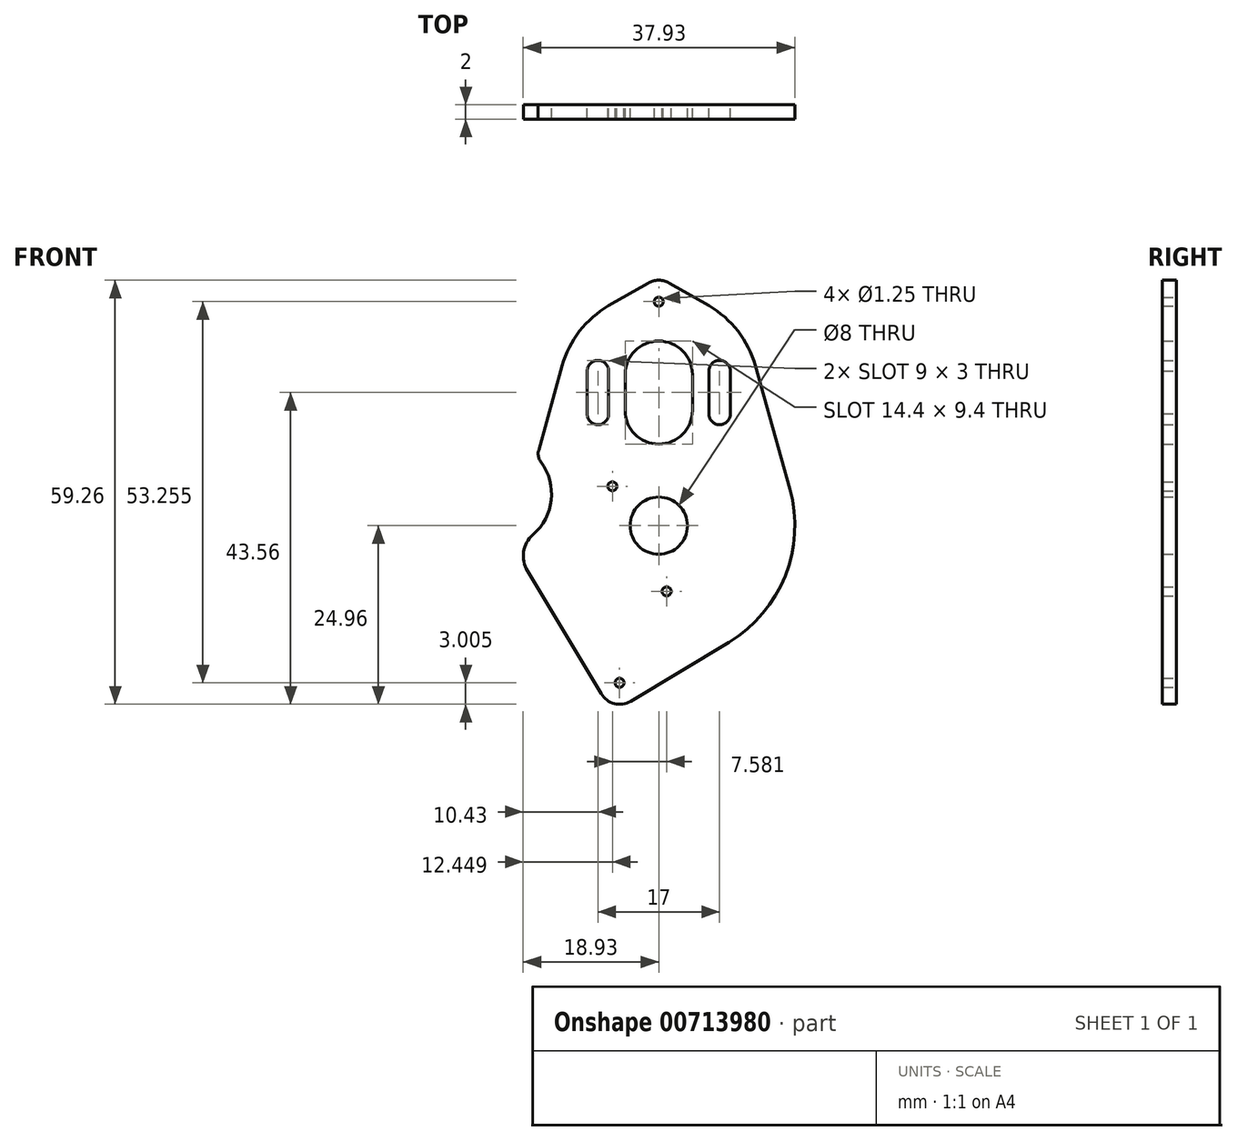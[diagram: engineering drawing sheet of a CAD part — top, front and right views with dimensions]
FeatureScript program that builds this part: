
annotation { "Feature Type Name" : "Feature", "Feature Type Description" : "" }
export const myFeature = defineFeature(function(context is Context, id is Id, definition is map)
    precondition{}
    {
        {
            var Q0;
            Q0=qCreatedBy(makeId("Front.planeOp"),FACE);
            var sketch = newSketch(context, id + "F0", { "sketchPlane" : qUnion([Q0])});
            skCircle(sketch, "E0", {"center": v(0, 0) * mm, "radius": 4 * mm});
            skArc(sketch, "E1", {"start": v(9.79, -16.29) * mm, "mid": v(17.65, -7.03) * mm, "end": v(18.3, 5.1) * mm});
            skLineSegment(sketch, "E2", {"start": v(-18.36, -6.34) * mm, "end": v(-8.05, -23.5) * mm});
            skLineSegment(sketch, "E3", {"start": v(-3.93, -24.53) * mm, "end": v(9.79, -16.29) * mm});
            skCircle(sketch, "E4", {"center": v(0, 0) * mm, "radius": 9.25 * mm, "construction": true});
            skCircle(sketch, "E5", {"center": v(1.1, -9.18) * mm, "radius": 0.62 * mm});
            skCircle(sketch, "E6", {"center": v(0, 0) * mm, "radius": 8.5 * mm, "construction": true});
            skCircle(sketch, "E7", {"center": v(-6.48, 5.5) * mm, "radius": 0.62 * mm});
            skArc(sketch, "E8", {"start": v(-4.7, 16.1) * mm, "mid": v(0, 11.4) * mm, "end": v(4.7, 16.1) * mm});
            skLineSegment(sketch, "E9", {"start": v(0, 0) * mm, "end": v(0, 43.43) * mm, "construction": true});
            skLineSegment(sketch, "E10", {"start": v(4.7, 16.1) * mm, "end": v(4.7, 21.1) * mm});
            skLineSegment(sketch, "E11", {"start": v(-4.7, 16.1) * mm, "end": v(-4.7, 21.1) * mm});
            skArc(sketch, "E12.trimOffspring", {"start": v(4.7, 21.1) * mm, "mid": v(0, 25.8) * mm, "end": v(-4.7, 21.1) * mm});
            skArc(sketch, "E13", {"start": v(13.48, 22.36) * mm, "mid": v(11.06, 27.18) * mm, "end": v(7, 30.73) * mm});
            skLineSegment(sketch, "E14", {"start": v(13.48, 22.36) * mm, "end": v(18.3, 5.1) * mm});
            skLineSegment(sketch, "E15.MirrorCS", {"start": v(-13.48, 22.36) * mm, "end": v(-16.77, 10.6) * mm});
            skArc(sketch, "E16", {"start": v(-17.55, -1.26) * mm, "mid": v(-15.02, 3.58) * mm, "end": v(-16.45, 8.86) * mm});
            skArc(sketch, "E17.filletArc", {"start": v(-17.55, -1.26) * mm, "mid": v(-18.88, -3.66) * mm, "end": v(-18.36, -6.34) * mm});
            skLineSegment(sketch, "E18", {"start": v(-17.05, 9.58) * mm, "end": v(-22.26, -9.08) * mm, "construction": true});
            skLineSegment(sketch, "E19", {"start": v(-18.36, -6.34) * mm, "end": v(-20.5, -2.77) * mm, "construction": true});
            skPoint(sketch, "E20.visualSharp", {"position": v(-17.05, 9.58) * mm});
            skArc(sketch, "E20.filletArc", {"start": v(-16.77, 10.6) * mm, "mid": v(-16.81, 9.7) * mm, "end": v(-16.45, 8.86) * mm});
            skCircle(sketch, "E21", {"center": v(-5.47, -21.96) * mm, "radius": 0.62 * mm});
            skPoint(sketch, "E22.visualSharp", {"position": v(-6.5, -26.07) * mm});
            skArc(sketch, "E22.filletArc", {"start": v(-8.05, -23.5) * mm, "mid": v(-6.2, -24.87) * mm, "end": v(-3.93, -24.53) * mm});
            skLineSegment(sketch, "E23", {"start": v(-8.29, 18.6) * mm, "end": v(14.54, 18.6) * mm, "construction": true});
            skArc(sketch, "E24", {"start": v(7, 15.6) * mm, "mid": v(8.5, 14.1) * mm, "end": v(10, 15.62) * mm});
            skLineSegment(sketch, "E25", {"start": v(7, 15.6) * mm, "end": v(7, 18.6) * mm});
            skLineSegment(sketch, "E26", {"start": v(10, 15.58) * mm, "end": v(10, 18.6) * mm});
            skLineSegment(sketch, "E27.MirrorCS", {"start": v(10, 21.62) * mm, "end": v(10, 18.6) * mm});
            skLineSegment(sketch, "E28.MirrorCS", {"start": v(7, 21.6) * mm, "end": v(7, 18.6) * mm});
            skArc(sketch, "E29.MirrorCS", {"start": v(7, 21.6) * mm, "mid": v(8.5, 23.1) * mm, "end": v(10, 21.58) * mm});
            skArc(sketch, "E30.MirrorCS", {"start": v(-7, 21.6) * mm, "mid": v(-8.5, 23.1) * mm, "end": v(-10, 21.58) * mm});
            skArc(sketch, "E31.MirrorCS", {"start": v(-7, 15.6) * mm, "mid": v(-8.5, 14.1) * mm, "end": v(-10, 15.62) * mm});
            skLineSegment(sketch, "E32.MirrorCS", {"start": v(-7, 15.6) * mm, "end": v(-7, 18.6) * mm});
            skLineSegment(sketch, "E33.MirrorCS", {"start": v(-10, 15.58) * mm, "end": v(-10, 18.6) * mm});
            skLineSegment(sketch, "E34.MirrorCS", {"start": v(-10, 21.62) * mm, "end": v(-10, 18.6) * mm});
            skLineSegment(sketch, "E35.MirrorCS", {"start": v(-7, 21.6) * mm, "end": v(-7, 18.6) * mm});
            skCircle(sketch, "E36", {"center": v(0, 31.3) * mm, "radius": 0.62 * mm});
            skArc(sketch, "E37", {"start": v(1.5, 33.9) * mm, "mid": v(0, 34.3) * mm, "end": v(-1.5, 33.9) * mm});
            skArc(sketch, "E38.trimOffspring", {"start": v(-7, 30.73) * mm, "mid": v(-11.06, 27.18) * mm, "end": v(-13.48, 22.36) * mm});
            skLineSegment(sketch, "E39", {"start": v(0, 0) * mm, "end": v(-16.29, -9.79) * mm, "construction": true});
            skLineSegment(sketch, "E40", {"start": v(-1.5, 33.9) * mm, "end": v(-7, 30.73) * mm});
            skLineSegment(sketch, "E41", {"start": v(1.5, 33.9) * mm, "end": v(7, 30.73) * mm});
            skLineSegment(sketch, "E42", {"start": v(0, 0) * mm, "end": v(-6.48, 5.5) * mm, "construction": true});
            skSolve(sketch);
        }
        {
            var Q0;
            Q0=makeQuery(id+"F0.imprint","IMPRINT",FACE,{"disambiguationData":[TD([[makeQuery(id+"F0.imprint","IMPRINT",EDGE,{"derivedFrom":sQuery(id+"F0.wireOp",EDGE,"E0")}),-1.0]])]});
            extrude(context, id + "F1", {"entities" : qUnion([Q0]), "depth" : 2 * mm, "offsetDistance" : 25 * mm});
        }
    });
